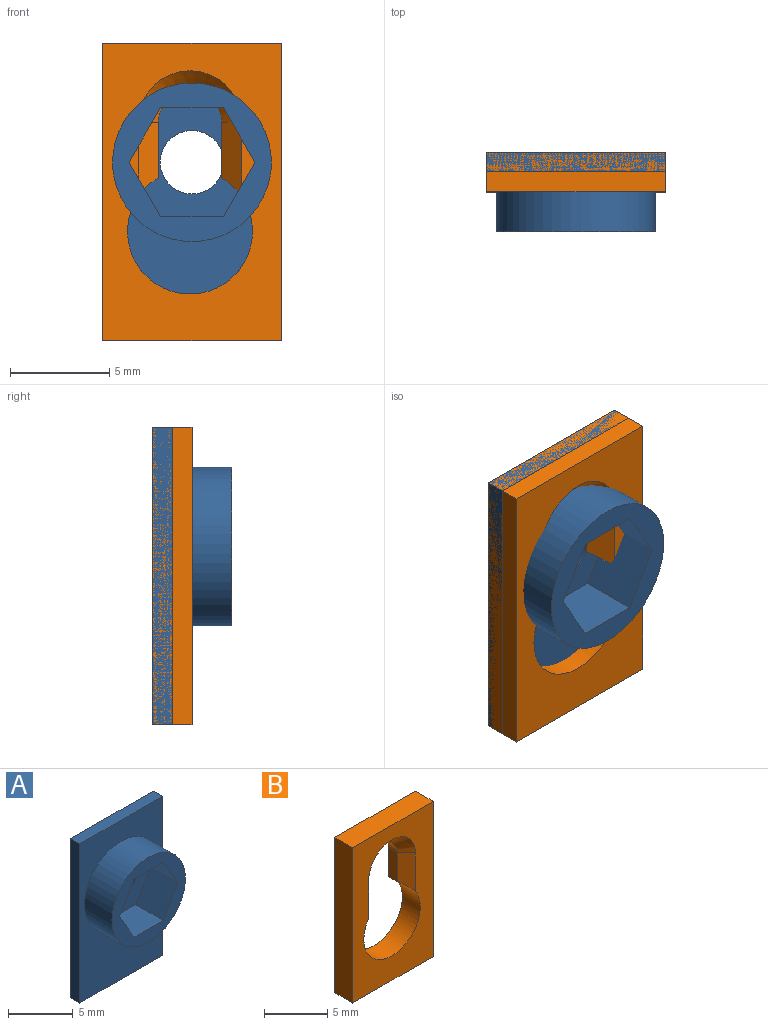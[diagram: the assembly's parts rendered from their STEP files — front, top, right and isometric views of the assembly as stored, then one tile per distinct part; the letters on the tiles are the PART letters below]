
ASSEMBLY  parts=2 mates=1
PART A: 16 faces, bbox 9x4x15 mm
  f0: plane 6.35x5.5mm, normal (0,-1,0), area 18.2mm2, adj f5,f8,f9,f10,f11,f12,f13
  f1: plane 15x1mm, normal (-1,0,0), area 15mm2, adj f2,f4,f6,f7
  f2: plane 9x1mm, normal (0,0,-1), area 9mm2, adj f1,f3,f6,f7
  f3: plane 15x1mm, normal (1,0,0), area 15mm2, adj f2,f4,f6,f7
  f4: plane 9x1mm, normal (0,0,1), area 9mm2, adj f1,f3,f6,f7
  f5: cylinder r=1.6mm len=3.2mm, axis (0,-1,0), area 10.1mm2, adj f0,f6
  f6: plane 15x9mm, normal (0,1,0), area 127mm2, adj f1,f2,f3,f4,f5
  f7: plane 15x9mm, normal (0,-1,0), area 84.7mm2, adj f1,f2,f3,f4,f14
  f8: plane 3.18x3mm, normal (0,0,-1), area 9.5mm2, adj f0,f9,f13,f15
  f9: plane 3x2.75mm, normal (-0.87,0,-0.5), area 9.5mm2, adj f0,f8,f10,f15
  f10: plane 3x2.75mm, normal (-0.87,0,0.5), area 9.5mm2, adj f0,f9,f11,f15
  f11: plane 3.18x3mm, normal (0,0,1), area 9.5mm2, adj f0,f10,f12,f15
  f12: plane 3x2.75mm, normal (0.87,0,0.5), area 9.5mm2, adj f0,f11,f13,f15
  f13: plane 3x2.75mm, normal (0.87,0,-0.5), area 9.5mm2, adj f0,f8,f12,f15
  f14: cylinder r=4mm len=8mm, axis (0,1,0), area 75.4mm2, adj f7,f15
  f15: plane 8x8mm, normal (0,-1,0), area 24.1mm2, adj f8,f9,f10,f11,f12,f13,f14
PART B: 13 faces, bbox 9x2x15 mm
  f0: cylinder r=3.15mm len=6.3mm, axis (0,1,0), area 31.6mm2, adj f1,f7,f8,f9,f10,f12
  f1: plane 2.79x1mm, normal (1,0,0), area 2.8mm2, adj f0,f2,f9,f10
  f2: cylinder r=1.6mm len=3.2mm, axis (0,1,0), area 5mm2, adj f1,f7,f9,f11
  f3: plane 15x2mm, normal (-1,0,0), area 30mm2, adj f4,f6,f8,f9
  f4: plane 9x2mm, normal (0,0,-1), area 18mm2, adj f3,f5,f8,f9
  f5: plane 15x2mm, normal (1,0,0), area 30mm2, adj f4,f6,f8,f9
  f6: plane 9x2mm, normal (0,0,1), area 18mm2, adj f3,f5,f8,f9
  f7: plane 2.79x1mm, normal (-1,0,0), area 2.8mm2, adj f0,f2,f9,f12
  f8: plane 15x9mm, normal (0,-1,0), area 78.9mm2, adj f0,f3,f4,f5,f6,f10,f11,f12
  f9: plane 15x9mm, normal (0,1,0), area 91.8mm2, adj f0,f1,f2,f3,f4,f5,f6,f7
  f10: plane 3.72x1mm, normal (0.71,-0.71,0), area 4.5mm2, adj f0,f1,f8,f11
  f11: cone r=1.6mm half-angle=45deg, axis (0,-1,0), area 9.3mm2, adj f2,f8,f10,f12
  f12: plane 3.72x1mm, normal (-0.71,-0.71,0), area 4.5mm2, adj f0,f7,f8,f11
PLACE A t=(-0.87,3.27,1.72)mm
PLACE B t=(-0.87,4.27,1.72)mm
MATE fastened B.f9 <-> A.f6  axis (0,1,0) through (3.63,4.27,16.72)mm
